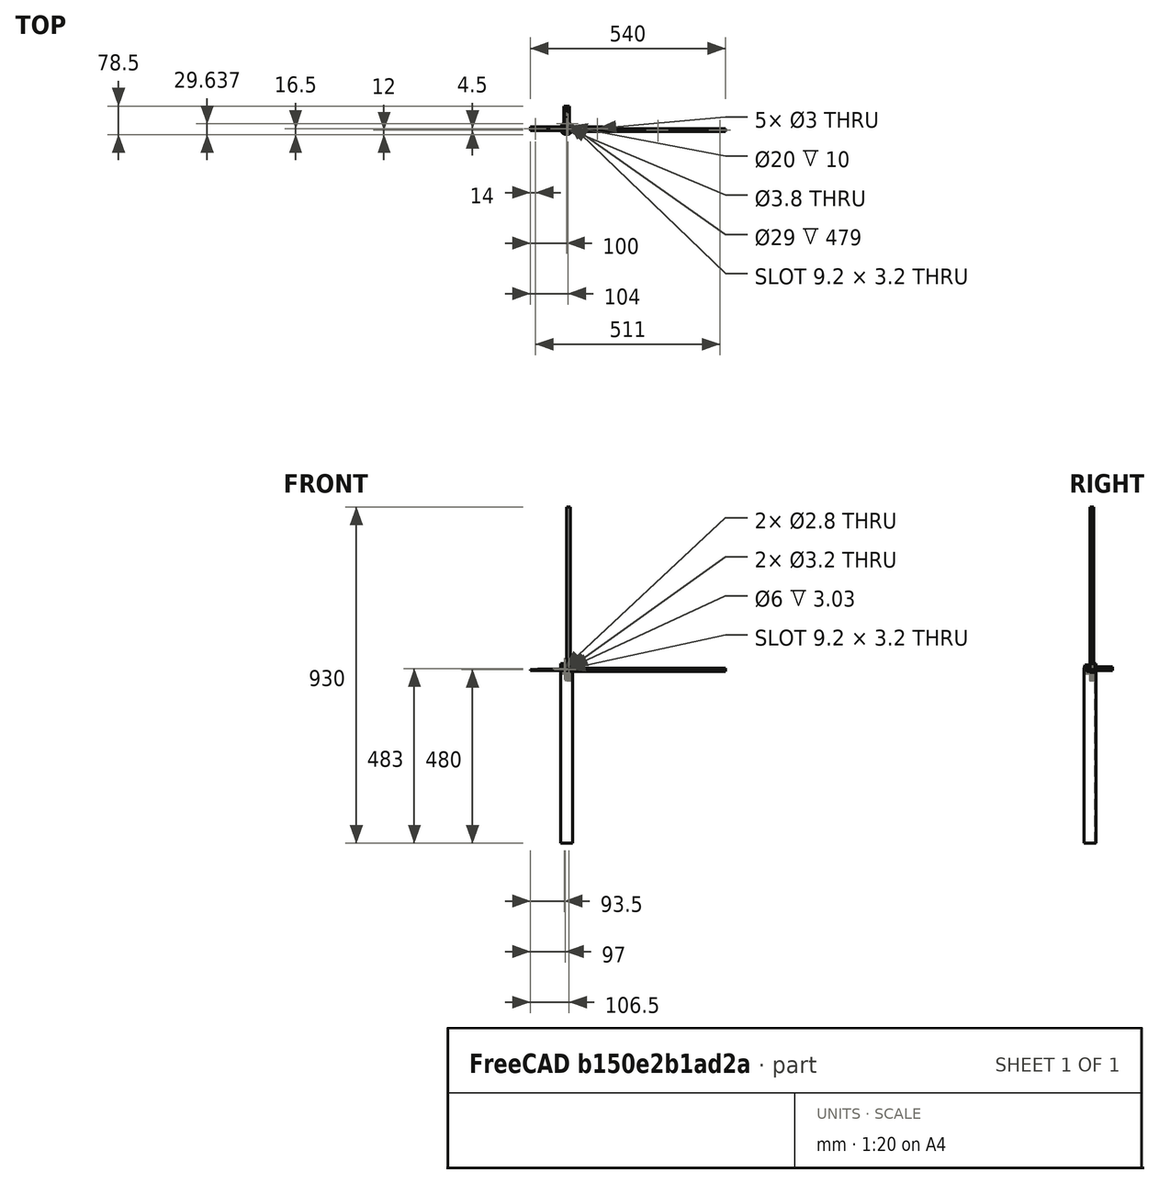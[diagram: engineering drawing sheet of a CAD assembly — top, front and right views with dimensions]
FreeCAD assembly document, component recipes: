
FREECAD ASSEMBLY — COMPONENT RECIPES ("angleBarLamp")

This assembly document has 14 components, labeled P0..P13 below (a component is one placed body or linked part). 13 of them carry a construction recipe — the FreeCAD feature program that regenerates the part from scratch, quoted from this document or its linked companion documents; the rest are supplied as boundary geometry only. No exploded tour is included for this assembly.
COMPONENT P0 — geometry summary ("Assembly"; no construction recipe available for this part):
  bounding box: 1011.0 x 58.0 x 58.0 mm
  tessellated surface: 14,300 triangles
  volume: 263663 mm^3 (8% of its bounding box)
COMPONENT P1 — recipe-attached ("b_cableClip", modeled in this document).
Construction recipe (the document's own serialized feature program — sketch geometry with constraints, then the solid features built on it; lengths are millimeters unless a unit is written):

FEATURE [PartDesign::CoordinateSystem] LCS_1
  AttacherType = Attacher::AttachEngine3D
  MapMode = 2
  Support = -> [X_Axis028]
FEATURE [Sketcher::SketchObject] Sketch028  label="sk_cableClipProfile"
  FullyConstrained = true
  MapMode = 5
  Support = -> [XY_Plane028]
  sketch-geometry (30):
    g0: LineSegment StartX=0 StartY=0 StartZ=0 EndX=0 EndY=10.1 EndZ=0
    g1: LineSegment StartX=0 StartY=10.1 StartZ=0 EndX=1.2 EndY=10.1 EndZ=0
    g2: LineSegment StartX=1.2 StartY=10.1 StartZ=0 EndX=1.2 EndY=1.2 EndZ=0
    g3: LineSegment StartX=1.2 StartY=1.2 StartZ=0 EndX=10.1 EndY=1.2 EndZ=0
    g4: LineSegment StartX=10.1 StartY=1.2 StartZ=0 EndX=10.1 EndY=0 EndZ=0
    g5: LineSegment StartX=10.1 StartY=0 StartZ=0 EndX=0 EndY=0 EndZ=0
    g6: LineSegment StartX=6.1 StartY=1.2 StartZ=0 EndX=6.1 EndY=2.7 EndZ=0
    g7: LineSegment StartX=6.1 StartY=2.7 StartZ=0 EndX=11.6 EndY=2.7 EndZ=0
    g8: LineSegment StartX=11.6 StartY=2.7 StartZ=0 EndX=11.6 EndY=-1.5 EndZ=0
    g9: LineSegment StartX=11.6 StartY=-1.5 StartZ=0 EndX=10.05 EndY=-1.5 EndZ=0
    g10: LineSegment StartX=-1.5 StartY=-1.5 StartZ=0 EndX=-1.5 EndY=5 EndZ=0
    g11: LineSegment StartX=-1.5 StartY=5 StartZ=0 EndX=0 EndY=5 EndZ=0
    g12: LineSegment StartX=0 StartY=5 StartZ=0 EndX=0 EndY=0 EndZ=0
    g13: LineSegment StartX=0 StartY=0 StartZ=0 EndX=1.55 EndY=0 EndZ=0
    g14: LineSegment StartX=10.1 StartY=0 StartZ=0 EndX=10.1 EndY=1.2 EndZ=0
    g15: LineSegment StartX=10.1 StartY=1.2 StartZ=0 EndX=6.1 EndY=1.2 EndZ=0
    g16: LineSegment StartX=-1.5 StartY=-1.5 StartZ=0 EndX=0 EndY=0 EndZ=0
    g17: LineSegment StartX=11.6 StartY=2.7 StartZ=0 EndX=10.1 EndY=1.2 EndZ=0
    g18: LineSegment StartX=1.55 StartY=0 StartZ=0 EndX=1.55 EndY=-2.5 EndZ=0
    g19: LineSegment StartX=1.55 StartY=-2.5 StartZ=0 EndX=8.55 EndY=-2.5 EndZ=0
    g20: LineSegment StartX=8.55 StartY=-2.5 StartZ=0 EndX=8.55 EndY=0 EndZ=0
    g21: LineSegment StartX=10.05 StartY=-1.5 StartZ=0 EndX=10.05 EndY=-4 EndZ=0
    g22: LineSegment StartX=10.05 StartY=-4 StartZ=0 EndX=0.05 EndY=-4 EndZ=0
    g23: LineSegment StartX=0.05 StartY=-4 StartZ=0 EndX=0.05 EndY=-1.5 EndZ=0
    g24: LineSegment StartX=8.55 StartY=0 StartZ=0 EndX=10.1 EndY=0 EndZ=0
    g25: LineSegment StartX=0.05 StartY=-1.5 StartZ=0 EndX=-1.5 EndY=-1.5 EndZ=0
    g26: LineSegment StartX=0.05 StartY=-1.5 StartZ=0 EndX=1.55 EndY=0 EndZ=0
    g27: LineSegment StartX=8.55 StartY=0 StartZ=0 EndX=10.05 EndY=-1.5 EndZ=0
    g28: LineSegment StartX=8.55 StartY=-2.5 StartZ=0 EndX=10.05 EndY=-4 EndZ=0
    g29: LineSegment StartX=0.05 StartY=-4 StartZ=0 EndX=1.55 EndY=-2.5 EndZ=0
  constraints (78):
    c: Coincident(g0,g1)
    c: Coincident(g1,g2)
    c: Coincident(g2,g3)
    c: Coincident(g3,g4)
    c: Coincident(g4,g5)
    c: Coincident(g0,g5)
    c: Coincident(g0,g-1)
    c: Horizontal(g1)
    c: Horizontal(g3)
    c: Horizontal(g5)
    c: Vertical(g0)
    c: Vertical(g2)
    c: Vertical(g4)
    c: Equal(g1,g4)
    c: Equal(g5,g0)
    c: DistanceX(g5,g5) = 10.1
    c: DistanceY(g4,g4) = 1.2
    c: Coincident(g6,g7)
    c: Coincident(g7,g8)
    c: Coincident(g8,g9)
    c: Coincident(g25,g10)
    c: Coincident(g10,g11)
    c: Coincident(g11,g12)
    c: Coincident(g12,g13)
    c: Coincident(g24,g14)
    c: Coincident(g14,g15)
    c: Coincident(g15,g6)
    c: Coincident(g3,g14)
    c: Coincident(g4,g24)
    c: PointOnObject(g6,g3)
    c: PointOnObject(g11,g0)
    c: Coincident(g0,g12)
    c: Vertical(g8)
    c: Vertical(g6)
    c: Horizontal(g9)
    c: Horizontal(g11)
    c: Horizontal(g7)
    c: Equal(g11,g6)
    c: DistanceX(g11,g11) = 1.5
    c: Vertical(g10)
    c: Coincident(g17,g14)
    c: Coincident(g17,g7)
    c: Angle(g7,g17) = 0.785398
    c: Angle(g16,g10) = 0.785398
    c: Coincident(g25,g16)
    c: Coincident(g0,g16)
    c: DistanceX(g15,g15) = 4
    c: DistanceY(g12,g12) = 5
    c: Coincident(g18,g19)
    c: Coincident(g19,g20)
    c: Coincident(g21,g22)
    c: Coincident(g22,g23)
    c: Coincident(g13,g18)
    c: Coincident(g24,g20)
    c: Tangent(g13,g24)
    c: Coincident(g9,g21)
    c: Tangent(g9,g25)
    c: Vertical(g23)
    c: Vertical(g18)
    c: Vertical(g20)
    c: Vertical(g21)
    c: Horizontal(g19)
    c: Horizontal(g22)
    c: DistanceX(g19,g19) = 7
    c: Coincident(g18,g29)
    c: Coincident(g22,g29)
    c: Coincident(g19,g28)
    c: Coincident(g21,g28)
    c: Coincident(g20,g27)
    c: Coincident(g9,g27)
    c: Parallel(g16,g26)
    c: Parallel(g26,g29)
    c: Coincident(g13,g26)
    c: Coincident(g23,g25)
    c: Coincident(g23,g26)
    c: Angle(g28,g22) = 0.785398
    c: Equal(g13,g24)
    c: DistanceY(g20,g20) = 2.5
FEATURE [PartDesign::Pad] Pad010  label="cableClipExtrude"
  AllowMultiFace = false
  Direction = (1,1,1)
  Length = 10
  Length2 = 100
  Profile = -> Sketch028
  Refine = true
  Type = 0
FEATURE [PartDesign::Fillet] Fillet002  label="cableClipFillet"
  Base = -> Pad010 [Edge23,Edge17,Edge14,Edge8,Edge11,Edge5,Edge26,Edge2,Edge20]
  BaseFeature = -> Pad010
  Radius = 0.5
  Refine = true
  SupportTransform = true
  UseAllEdges = false
FEATURE [PartDesign::Body] Body  label="b_cableClip"
  Group = -> [Sketch028,Pad010,Fillet002,LCS_1]
  Origin = -> Origin028
  Tip = -> Fillet002
COMPONENT P2 — recipe-attached ("template_L-profile_10mm_foot", modeled in this document).
Construction recipe (the document's own serialized feature program — sketch geometry with constraints, then the solid features built on it; lengths are millimeters unless a unit is written):

FEATURE [PartDesign::CoordinateSystem] LCS_angleBar10  label="LCS_Lprofile10"
  AttacherType = Attacher::AttachEngine3D
  MapMode = 2
  Support = -> [X_Axis006]
FEATURE [Sketcher::SketchObject] Sketch017  label="sk_L-profile10mm"
  FullyConstrained = false
  MapMode = 5
  Support = -> [XY_Plane006]
  sketch-geometry (6):
    g0: LineSegment StartX=0 StartY=0 StartZ=0 EndX=0 EndY=10.1 EndZ=0
    g1: LineSegment StartX=0 StartY=10.1 StartZ=0 EndX=1.1 EndY=10.1 EndZ=0
    g2: LineSegment StartX=1.1 StartY=10.1 StartZ=0 EndX=1.1 EndY=1.1 EndZ=0
    g3: LineSegment StartX=1.1 StartY=1.1 StartZ=0 EndX=10.1 EndY=1.1 EndZ=0
    g4: LineSegment StartX=10.1 StartY=1.1 StartZ=0 EndX=10.1 EndY=0 EndZ=0
    g5: LineSegment StartX=10.1 StartY=0 StartZ=0 EndX=0 EndY=0 EndZ=0
  constraints (17):
    c: Coincident(g-1,g0)
    c: PointOnObject(g0,g-2)
    c: Coincident(g0,g1)
    c: Horizontal(g1)
    c: Coincident(g1,g2)
    c: Vertical(g2)
    c: Coincident(g2,g3)
    c: Horizontal(g3)
    c: Coincident(g3,g4)
    c: Coincident(g4,g5)
    c: Coincident(g5,g0)
    c: Horizontal(g5)
    c: Vertical(g4)
    c: DistanceY(g0,g0) = 10.1
    c: Equal(g0,g5)
    c: DistanceX(g1,g1) = 1.1
    c: Equal(g1,g4)
FEATURE [PartDesign::Pad] Pad005  label="L-profile10mm"
  AllowMultiFace = false
  Direction = (0,0,1)
  Length = 450
  Length2 = 100
  Profile = -> Sketch017
  Type = 0
  expr: Length = Spreadsheet.l_arms
FEATURE [PartDesign::Body] Body006  label="template_L-profile_10mm_foot"
  Group = -> [Sketch017,Pad005,LCS_angleBar10]
  Origin = -> Origin006
  Tip = -> Pad005
COMPONENT P3 — recipe-attached ("b_base_cap", modeled in this document).
Construction recipe (the document's own serialized feature program — sketch geometry with constraints, then the solid features built on it; lengths are millimeters unless a unit is written):

FEATURE [PartDesign::CoordinateSystem] LCS_bottom_blog
  AttacherType = Attacher::AttachEngine3D
  AttachmentOffset = pos=(5,0,0) rot=(0,0,1;0rad)
  MapMode = 2
  Placement = pos=(1.1e-15,1.1e-15,5) rot=(0.57735,-0.57735,0.57735;2.0944rad)
  Support = -> [Z_Axis030]
FEATURE [Sketcher::SketchObject] Sketch001
  FullyConstrained = false
  MapMode = 5
  Placement = pos=(0,0,0) rot=(1,0,0;1.5708rad)
  Support = -> [XZ_Plane001]
  sketch-geometry (4):
    g0: LineSegment StartX=0 StartY=28.2609 StartZ=0 EndX=10 EndY=28.2609 EndZ=0
    g1: LineSegment StartX=10 StartY=28.2609 StartZ=0 EndX=10 EndY=3 EndZ=0
    g2: LineSegment StartX=10 StartY=3 StartZ=0 EndX=0 EndY=3 EndZ=0
    g3: LineSegment StartX=0 StartY=3 StartZ=0 EndX=0 EndY=28.2609 EndZ=0
  constraints (11):
    c: Coincident(g0,g1)
    c: Coincident(g1,g2)
    c: Coincident(g2,g3)
    c: Coincident(g3,g0)
    c: Horizontal(g0)
    c: Horizontal(g2)
    c: Vertical(g1)
    c: Vertical(g3)
    c: PointOnObject(g0,g-2)
    c: DistanceY(g1) = 3
    c: DistanceX(g0,g0) = 10
FEATURE [Sketcher::SketchObject] Sketch052
  FullyConstrained = true
  MapMode = 5
  Placement = pos=(0,0,0) rot=(1,0,0;1.5708rad)
  Support = -> [XZ_Plane001]
  sketch-geometry (6):
    g0: LineSegment StartX=0 StartY=0 StartZ=0 EndX=16.25 EndY=0 EndZ=0
    g1: LineSegment StartX=16.25 StartY=0 StartZ=0 EndX=16.25 EndY=5 EndZ=0
    g2: LineSegment StartX=16.25 StartY=5 StartZ=0 EndX=15 EndY=5 EndZ=0
    g3: LineSegment StartX=15 StartY=5 StartZ=0 EndX=15 EndY=13 EndZ=0
    g4: LineSegment StartX=15 StartY=13 StartZ=0 EndX=0 EndY=13 EndZ=0
    g5: LineSegment StartX=0 StartY=13 StartZ=0 EndX=0 EndY=0 EndZ=0
  constraints (17):
    c: Coincident(g-1,g0)
    c: Horizontal(g0)
    c: Coincident(g0,g1)
    c: Coincident(g1,g2)
    c: Horizontal(g2)
    c: Coincident(g2,g3)
    c: Coincident(g3,g4)
    c: Horizontal(g4)
    c: Coincident(g4,g5)
    c: Coincident(g5,g0)
    c: Vertical(g5)
    c: Vertical(g1)
    c: Vertical(g3)
    c: DistanceY(g3,g3) = 8
    c: DistanceY(g1,g1) = 5
    c: DistanceX(g4,g4) = 15
    c: DistanceX(g0,g0) = 16.25
FEATURE [PartDesign::Revolution] Revolution001
  Angle = 360
  Axis = (0,2e-16,1)
  Base = (0,0,0)
  Placement = pos=(0,0,0) rot=(1,0,0;1.5708rad)
  Profile = -> Sketch052
  ReferenceAxis = -> Sketch052 [V_Axis]
  Reversed = true
FEATURE [PartDesign::Chamfer] Chamfer001
  Angle = 3
  Base = -> Revolution001 [Edge5]
  BaseFeature = -> Revolution001
  ChamferType = 2
  FlipDirection = false
  Placement = pos=(0,0,0) rot=(1,0,0;1.5708rad)
  Size = 7
  Size2 = 1
  SupportTransform = false
  UseAllEdges = false
FEATURE [PartDesign::Groove] Groove001
  Angle = 360
  Axis = (0,2e-16,1)
  Base = (0,0,0)
  BaseFeature = -> Chamfer001
  Placement = pos=(0,0,0) rot=(1,0,0;1.5708rad)
  Profile = -> Sketch001
  ReferenceAxis = -> Sketch001 [V_Axis]
FEATURE [PartDesign::Body] Body015  label="b_base_cap"
  Group = -> [Sketch052,Revolution001,Chamfer001,Sketch001,Groove001,LCS_bottom_blog]
  Origin = -> Origin030
  Tip = -> Groove001
COMPONENT P4 — recipe-attached ("b_LProfile_8mm", modeled in this document).
Construction recipe (the document's own serialized feature program — sketch geometry with constraints, then the solid features built on it; lengths are millimeters unless a unit is written):

FEATURE [PartDesign::CoordinateSystem] LCS_1004  label="LCS_screwaxis"
  AttacherType = Attacher::AttachEngine3D
  MapMode = 2
  Support = -> [X_Axis031]
  expr: .AttachmentOffset.Base.x = Variables.time < Variables.motion2_start ? 0 : (Variables.time < Variables.motion3_start ? -Spreadsheet.l_sliding_hole * (Variables.time - Variables.motion2_start) / Variables.motion2_duration : -Spreadsheet.l_sliding_hole)
FEATURE [Sketcher::SketchObject] Sketch053
  FullyConstrained = true
  MapMode = 5
  Placement = pos=(0,0,0) rot=(0.57735,0.57735,0.57735;2.0944rad)
  Support = -> [YZ_Plane031]
  sketch-geometry (6):
    g0: LineSegment StartX=0 StartY=-4.5 StartZ=0 EndX=-8 EndY=-4.5 EndZ=0
    g1: LineSegment StartX=-8 StartY=-4.5 StartZ=0 EndX=-8 EndY=-3.5 EndZ=0
    g2: LineSegment StartX=-8 StartY=-3.5 StartZ=0 EndX=-1 EndY=-3.5 EndZ=0
    g3: LineSegment StartX=-1 StartY=-3.5 StartZ=0 EndX=-1 EndY=3.5 EndZ=0
    g4: LineSegment StartX=-1 StartY=3.5 StartZ=0 EndX=0 EndY=3.5 EndZ=0
    g5: LineSegment StartX=0 StartY=3.5 StartZ=0 EndX=0 EndY=-4.5 EndZ=0
  constraints (17):
    c: PointOnObject(g0,g-2)
    c: Horizontal(g0)
    c: Coincident(g0,g1)
    c: Coincident(g1,g2)
    c: Coincident(g2,g3)
    c: Coincident(g3,g4)
    c: PointOnObject(g4,g-2)
    c: Horizontal(g4)
    c: Coincident(g4,g5)
    c: Coincident(g5,g0)
    c: Equal(g1,g4)
    c: Vertical(g1)
    c: Equal(g0,g5)
    c: DistanceY(g5,g5) = 8
    c: DistanceY(g1,g1) = 1
    c: Horizontal(g2)
    c: Symmetric(g2,g3,g-1)
FEATURE [PartDesign::Pad] Pad017
  Direction = (1,-2e-16,3e-16)
  Length = 440
  Length2 = 16
  Placement = pos=(0,0,0) rot=(0.57735,0.57735,0.57735;2.0944rad)
  Profile = -> Sketch053
  ReferenceAxis = -> Sketch053 [N_Axis]
  Type = 4
FEATURE [Sketcher::SketchObject] Sketch054
  FullyConstrained = true
  MapMode = 5
  Placement = pos=(0,0,0) rot=(1,0,0;1.5708rad)
  Support = -> [XZ_Plane031]
  sketch-geometry (11):
    g0: ArcOfCircle CenterX=-6 CenterY=-1e-16 CenterZ=0 NormalX=0 NormalY=0 NormalZ=1 AngleXU=0 Radius=1.6 StartAngle=1.5708 EndAngle=4.71239
    g1: ArcOfCircle CenterX=0 CenterY=0 CenterZ=0 NormalX=0 NormalY=0 NormalZ=1 AngleXU=0 Radius=1.6 StartAngle=4.71239 EndAngle=7.85398
    g2: LineSegment StartX=-6 StartY=-1.6 StartZ=0 EndX=0 EndY=-1.6 EndZ=0
    g3: LineSegment StartX=5e-16 StartY=1.6 StartZ=0 EndX=-6 EndY=1.6 EndZ=0
    g4: LineSegment StartX=-16.5 StartY=4 StartZ=0 EndX=-10.5 EndY=4 EndZ=0
    g5: LineSegment StartX=-10.5 StartY=4 StartZ=0 EndX=-11.436 EndY=-0.3375 EndZ=0
    g6: ArcOfCircle CenterX=-13 CenterY=-1e-16 CenterZ=0 NormalX=0 NormalY=0 NormalZ=1 AngleXU=0 Radius=1.6 StartAngle=3.14159 EndAngle=6.07065
    g7: LineSegment StartX=-14.6 StartY=-6e-16 StartZ=0 EndX=-14.6 EndY=1.25 EndZ=0
    g8: ArcOfCircle CenterX=-15.1 CenterY=1.25 CenterZ=0 NormalX=0 NormalY=0 NormalZ=1 AngleXU=0 Radius=0.5 StartAngle=1e-16 EndAngle=1.75335
    g9: LineSegment StartX=-15.1908 StartY=1.74169 StartZ=0 EndX=-16.5 EndY=1.5 EndZ=0
    g10: LineSegment StartX=-16.5 StartY=1.5 StartZ=0 EndX=-16.5 EndY=4 EndZ=0
  constraints (28):
    c: Tangent(g0,g2) = -1.5708
    c: Tangent(g2,g1) = -1.5708
    c: Tangent(g1,g3) = -1.5708
    c: Tangent(g3,g0) = -1.5708
    c: Equal(g0,g1)
    c: Horizontal(g2)
    c: DistanceX(g3,g3) = 6
    c: Radius(g1) = 1.6
    c: Horizontal(g4)
    c: Coincident(g4,g5)
    c: Tangent(g5,g6) = 1.5708
    c: Tangent(g6,g7) = 1.5708
    c: Tangent(g7,g8) = -1.5708
    c: Coincident(g9,g10)
    c: Coincident(g10,g4)
    c: Vertical(g10)
    c: Vertical(g7)
    c: Radius(g6) = 1.6
    c: Tangent(g8,g9) = -1.5708
    c: Radius(g8) = 0.5
    c: DistanceY(g6,g8) = 1.25
    c: DistanceY(g8,g9) = 0.25
    c: Horizontal(g0,g6)
    c: DistanceX(g6,g0) = 7
    c: DistanceX(g6,g4) = 2.5
    c: DistanceX(g9,g6) = 3.5
    c: Coincident(g1,g-1)
    c: DistanceY(g6,g4) = 4
FEATURE [PartDesign::Pocket] Pocket018
  BaseFeature = -> Pad017
  Direction = (0,1,2e-16)
  Length = 5
  Length2 = 5
  Placement = pos=(0,0,0) rot=(0.57735,0.57735,0.57735;2.0944rad)
  Profile = -> Sketch054
  ReferenceAxis = -> Sketch054 [N_Axis]
  Reversed = true
  Type = 0
FEATURE [Sketcher::SketchObject] Sketch055
  FullyConstrained = true
  MapMode = 5
  Support = -> [XY_Plane031]
  expr: Constraints[2] = Spreadsheet.led_screw_offset
  expr: Constraints[5] = Spreadsheet.led_screw_pos
  sketch-geometry (2):
    g0: Circle CenterX=425 CenterY=-4.5 CenterZ=0 NormalX=0 NormalY=0 NormalZ=1 AngleXU=0 Radius=1.5
    g1: Circle CenterX=253 CenterY=-4.5 CenterZ=0 NormalX=0 NormalY=0 NormalZ=1 AngleXU=0 Radius=1.5
  constraints (6):
    c: Horizontal(g1,g0)
    c: Equal(g0,g1)
    c: DistanceX(g1,g0) = 172
    c: Diameter(g1) = 3
    c: DistanceY(g0,g-1) = 4.5
    c: DistanceX(g0) = 425
FEATURE [PartDesign::Pocket] Pocket019
  BaseFeature = -> Pocket018
  Direction = (0,0,-1)
  Length = 5
  Length2 = 5
  Placement = pos=(0,0,0) rot=(0.57735,0.57735,0.57735;2.0944rad)
  Profile = -> Sketch055
  ReferenceAxis = -> Sketch055 [N_Axis]
  Type = 0
FEATURE [PartDesign::CoordinateSystem] LCS_ledscrew
  AttacherType = Attacher::AttachEngine3D
  AttachmentOffset = pos=(425,-4.5,-4.5) rot=(0,0,1;0rad)
  MapMode = 2
  Placement = pos=(425,-4.5,-4.5) rot=(0,0,1;0rad)
  Support = -> [X_Axis031]
  expr: .AttachmentOffset.Base.x = Spreadsheet.led_screw_pos
FEATURE [PartDesign::Body] b_LProfile_8mm
  Group = -> [LCS_1004,Sketch053,Pad017,Sketch054,Pocket018,Sketch055,Pocket019,LCS_ledscrew]
  Origin = -> Origin031
  Tip = -> Pocket019
COMPONENT P5 — recipe-attached ("b_nut", modeled in this document).
Construction recipe (the document's own serialized feature program — sketch geometry with constraints, then the solid features built on it; lengths are millimeters unless a unit is written):

FEATURE [PartDesign::CoordinateSystem] LCS_0001
  AttacherType = Attacher::AttachEngine3D
  MapMode = 2
  Support = -> [X_Axis002]
FEATURE [Sketcher::SketchObject] Sketch037
  FullyConstrained = true
  MapMode = 5
  Placement = pos=(0,0,0) rot=(1,0,0;1.5708rad)
  Support = -> [XZ_Plane003]
  sketch-geometry (6):
    g0: LineSegment StartX=6.1 StartY=0.5 StartZ=0 EndX=6.1 EndY=2.8 EndZ=0
    g1: LineSegment StartX=6.1 StartY=0.5 StartZ=0 EndX=3 EndY=0.5 EndZ=0
    g2: LineSegment StartX=3 StartY=0.5 StartZ=0 EndX=3 EndY=0 EndZ=0
    g3: LineSegment StartX=6.1 StartY=2.8 StartZ=0 EndX=1.5 EndY=2.8 EndZ=0
    g4: LineSegment StartX=1.5 StartY=2.8 StartZ=0 EndX=1.5 EndY=0 EndZ=0
    g5: LineSegment StartX=1.5 StartY=0 StartZ=0 EndX=3 EndY=0 EndZ=0
  constraints (18):
    c: Vertical(g0)
    c: DistanceX(g-1,g0) = 6.1
    c: DistanceY(g0,g0) = 2.3
    c: Coincident(g0,g1)
    c: Horizontal(g1)
    c: Coincident(g1,g2)
    c: Vertical(g2)
    c: DistanceX(g-1,g2) = 3
    c: Coincident(g0,g3)
    c: Horizontal(g3)
    c: Coincident(g3,g4)
    c: Vertical(g4)
    c: Coincident(g4,g5)
    c: Coincident(g5,g2)
    c: Horizontal(g5)
    c: DistanceY(g4,g4) = 2.8
    c: DistanceX(g-1,g4) = 1.5
    c: PointOnObject(g4,g-1)
FEATURE [PartDesign::Revolution] Revolution
  Angle = 360
  Axis = (0,-2e-16,1)
  Base = (0,0,0)
  Placement = pos=(0,0,0) rot=(1,0,0;1.5708rad)
  Profile = -> Sketch037
  ReferenceAxis = -> Sketch037 [V_Axis]
  Reversed = true
FEATURE [Sketcher::SketchObject] Sketch038
  FullyConstrained = false
  MapMode = 5
  Support = -> [XY_Plane002]
  sketch-geometry (1):
    g0: Circle CenterX=0 CenterY=6.12912 CenterZ=0 NormalX=0 NormalY=0 NormalZ=1 AngleXU=0 Radius=0.15
  constraints (2):
    c: PointOnObject(g0,g-2)
    c: Radius(g0) = 0.15
FEATURE [PartDesign::Pocket] Pocket011
  BaseFeature = -> Revolution
  Direction = (1,1,1)
  Length = 5
  Length2 = 100
  Placement = pos=(0,0,0) rot=(1,0,0;1.5708rad)
  Profile = -> Sketch038
  Reversed = true
  Type = 1
FEATURE [PartDesign::PolarPattern] PolarPattern
  Angle = 360
  Axis = -> Sketch038 [N_Axis]
  BaseFeature = -> Pocket011
  Occurrences = 100
  Originals = -> [Pocket011]
  Placement = pos=(0,0,0) rot=(1,0,0;1.5708rad)
FEATURE [PartDesign::Body] b_nut
  Group = -> [LCS_0001,Sketch037,Revolution,Sketch038,Pocket011,PolarPattern]
  Origin = -> Origin002
  Tip = -> PolarPattern
COMPONENT P6 — recipe-attached ("b_spacer", modeled in this document).
Construction recipe (the document's own serialized feature program — sketch geometry with constraints, then the solid features built on it; lengths are millimeters unless a unit is written):

FEATURE [PartDesign::CoordinateSystem] LCS_0003
  AttacherType = Attacher::AttachEngine3D
  MapMode = 2
  Support = -> [X_Axis022]
FEATURE [Sketcher::SketchObject] Sketch034
  FullyConstrained = false
  MapMode = 5
  Support = -> [XY_Plane022]
  sketch-geometry (6):
    g0: Circle CenterX=0 CenterY=0 CenterZ=0 NormalX=0 NormalY=0 NormalZ=1 AngleXU=0 Radius=1.9
    g1: Circle CenterX=0 CenterY=0 CenterZ=0 NormalX=0 NormalY=0 NormalZ=1 AngleXU=0 Radius=2.7
    g2: LineSegment StartX=-2.74547 StartY=3.8 StartZ=0 EndX=7.25453 EndY=3.8 EndZ=0
    g3: LineSegment StartX=7.25453 StartY=3.8 StartZ=0 EndX=7.25453 EndY=-2.7 EndZ=0
    g4: LineSegment StartX=7.25453 StartY=-2.7 StartZ=0 EndX=-2.74547 EndY=-2.7 EndZ=0
    g5: LineSegment StartX=-2.74547 StartY=-2.7 StartZ=0 EndX=-2.74547 EndY=3.8 EndZ=0
  constraints (15):
    c: Coincident(g0,g-1)
    c: Coincident(g1,g0)
    c: Radius(g0) = 1.9
    c: Radius(g1) = 2.7
    c: Coincident(g2,g3)
    c: Coincident(g3,g4)
    c: Coincident(g4,g5)
    c: Coincident(g5,g2)
    c: Horizontal(g2)
    c: Horizontal(g4)
    c: Vertical(g3)
    c: Vertical(g5)
    c: DistanceY(g3,g3) = 6.5
    c: DistanceY(g4,g0) = 2.7
    c: DistanceX(g2,g2) = 10
FEATURE [PartDesign::Pad] Pad013
  Direction = (1,1,1)
  Length = 6.5
  Length2 = 100
  Profile = -> Sketch034
  Type = 0
FEATURE [PartDesign::Body] b_spacer
  Group = -> [LCS_0003,Sketch034,Pad013]
  Origin = -> Origin022
  Tip = -> Pad013
COMPONENT P7 — recipe-attached ("b_stencil", modeled in this document).
Construction recipe (the document's own serialized feature program — sketch geometry with constraints, then the solid features built on it; lengths are millimeters unless a unit is written):

FEATURE [PartDesign::CoordinateSystem] LCS_0005
  AttacherType = Attacher::AttachEngine3D
  MapMode = 2
  Support = -> [X_Axis024]
FEATURE [PartDesign::ShapeBinder] ShapeBinder
  Placement = pos=(0,0,1) rot=(0,0,1;3.14159rad)
  Support = -> [Sketch048]
  TraceSupport = false
FEATURE [Sketcher::SketchObject] Sketch049
  FullyConstrained = false
  MapMode = 5
  Placement = pos=(0,0,0) rot=(1,0,0;1.5708rad)
  Support = -> [XZ_Plane024]
  sketch-geometry (6):
    g0: LineSegment StartX=0 StartY=8 StartZ=0 EndX=0 EndY=0 EndZ=0
    g1: LineSegment StartX=0 StartY=0 StartZ=0 EndX=8 EndY=0 EndZ=0
    g2: LineSegment StartX=8 StartY=0 StartZ=0 EndX=8 EndY=-2.47577 EndZ=0
    g3: LineSegment StartX=8 StartY=-2.47577 StartZ=0 EndX=-7.32977 EndY=-2.47577 EndZ=0
    g4: LineSegment StartX=-7.32977 StartY=-2.47577 StartZ=0 EndX=-7.32977 EndY=8 EndZ=0
    g5: LineSegment StartX=-7.32977 StartY=8 StartZ=0 EndX=0 EndY=8 EndZ=0
  constraints (15):
    c: PointOnObject(g0,g-2)
    c: Coincident(g0,g-1)
    c: Coincident(g0,g1)
    c: PointOnObject(g1,g-1)
    c: Coincident(g1,g2)
    c: Vertical(g2)
    c: Coincident(g2,g3)
    c: Horizontal(g3)
    c: Coincident(g3,g4)
    c: Vertical(g4)
    c: Coincident(g4,g5)
    c: Coincident(g5,g0)
    c: Horizontal(g5)
    c: DistanceX(g1,g1) = 8
    c: Equal(g0,g1)
FEATURE [PartDesign::Pad] Pad014
  Direction = (1,1,1)
  Length = 62
  Length2 = 100
  Placement = pos=(0,0,0) rot=(1,0,0;1.5708rad)
  Profile = -> Sketch049
  Refine = true
  Reversed = true
  Type = 0
FEATURE [PartDesign::Pocket] Pocket017
  BaseFeature = -> Pad014
  Direction = (0,0,-1)
  Length = 5
  Length2 = 100
  Placement = pos=(0,0,0) rot=(1,0,0;1.5708rad)
  Profile = -> ShapeBinder
  Refine = true
  Type = 0
FEATURE [PartDesign::Body] b_stencil
  Group = -> [LCS_0005,ShapeBinder,Sketch049,Pad014,Pocket017]
  Origin = -> Origin024
  Tip = -> Pocket017
COMPONENT P8 — recipe-attached ("b_topBlockArmLock", modeled in this document).
Construction recipe (the document's own serialized feature program — sketch geometry with constraints, then the solid features built on it; lengths are millimeters unless a unit is written):

FEATURE [PartDesign::Plane] DatumPlane
  AttachmentOffset = pos=(0,0,12) rot=(0,0,1;0rad)
  Length = 60
  MapMode = 2
  Placement = pos=(4.7e-15,12,-4.7e-15) rot=(0.57735,0.57735,0.57735;4.18879rad)
  ResizeMode = 0
  Support = -> [Z_Axis001]
  Width = 60
FEATURE [PartDesign::CoordinateSystem] LCS_0
  AttacherType = Attacher::AttachEngine3D
  MapMode = 2
  Support = -> [X_Axis001]
FEATURE [Sketcher::SketchObject] Sketch
  FullyConstrained = true
  MapMode = 5
  Support = -> [XY_Plane001]
  expr: Constraints[16] = Spreadsheet.r_inner
  expr: Constraints[5] = Spreadsheet.w_topRail
  expr: Constraints[6] = Spreadsheet.w_wall_center / 2
  expr: Constraints[9] = Spreadsheet.r_outer
  sketch-geometry (7):
    g0: LineSegment StartX=-16.5 StartY=2e-15 StartZ=0 EndX=16.5 EndY=0 EndZ=0
    g1: ArcOfCircle CenterX=0 CenterY=0 CenterZ=0 NormalX=0 NormalY=0 NormalZ=1 AngleXU=0 Radius=16.5 StartAngle=0 EndAngle=2.22189
    g2: LineSegment StartX=-16.4829 StartY=0.75 StartZ=0 EndX=14.6058 EndY=0.75 EndZ=0
    g3: LineSegment StartX=11.6434 StartY=8.85 StartZ=0 EndX=-10 EndY=8.85 EndZ=0
    g4: LineSegment StartX=-10 StartY=8.85 StartZ=0 EndX=-10 EndY=13.1244 EndZ=0
    g5: ArcOfCircle CenterX=0 CenterY=0 CenterZ=0 NormalX=0 NormalY=0 NormalZ=1 AngleXU=0 Radius=16.5 StartAngle=3.09612 EndAngle=3.14159
    g6: ArcOfCircle CenterX=0 CenterY=0 CenterZ=0 NormalX=0 NormalY=0 NormalZ=1 AngleXU=0 Radius=14.625 StartAngle=0.0513046 EndAngle=0.649927
  constraints (20):
    c: PointOnObject(g0,g-1)
    c: Coincident(g1,g-1)
    c: Horizontal(g2)
    c: Horizontal(g3)
    c: Coincident(g3,g4)
    c: DistanceY(g2,g3) = 8.1
    c: DistanceY(g0,g2) = 0.75
    c: Vertical(g4)
    c: Symmetric(g0,g0,g1)
    c: Radius(g1) = 16.5
    c: Coincident(g1,g0)
    c: Coincident(g5,g1)
    c: Coincident(g5,g0)
    c: Coincident(g5,g2)
    c: Coincident(g6,g2)
    c: Coincident(g6,g3)
    c: Radius(g6) = 14.625
    c: Coincident(g1,g6)
    c: Coincident(g1,g4)
    c: DistanceX(g3,g1) = 10
FEATURE [PartDesign::Pad] Pad009
  Direction = (0,0,1)
  Length = 16
  Length2 = 7.5
  Profile = -> Sketch
  Type = 4
FEATURE [Sketcher::SketchObject] Sketch030
  FullyConstrained = true
  MapMode = 5
  Placement = pos=(0,0,0) rot=(1,0,0;1.5708rad)
  Support = -> [XZ_Plane002]
  expr: Constraints[6] = Spreadsheet.motionAngle
  sketch-geometry (3):
    g0: LineSegment StartX=6.5 StartY=-7.5 StartZ=0 EndX=-1.5 EndY=-7.5 EndZ=0
    g1: LineSegment StartX=-1.5 StartY=-7.5 StartZ=0 EndX=-1.5 EndY=-4.58824 EndZ=0
    g2: LineSegment StartX=-1.5 StartY=-4.58824 StartZ=0 EndX=6.5 EndY=-7.5 EndZ=0
  constraints (9):
    c: Horizontal(g0)
    c: DistanceY(g0,g-1) = 7.5
    c: Coincident(g0,g1)
    c: Vertical(g1)
    c: Coincident(g1,g2)
    c: Coincident(g0,g2)
    c: Angle(g2,g0) = 0.349066
    c: DistanceX(g0) = 6.5
    c: DistanceX(g0,g0) = 8
FEATURE [Sketcher::SketchObject] Sketch033
  FullyConstrained = false
  MapMode = 5
  Placement = pos=(4.7e-15,12,-4.7e-15) rot=(0.57735,0.57735,0.57735;4.18879rad)
  Support = -> [DatumPlane]
  expr: Constraints[0] = Spreadsheet.screw_offset
  sketch-geometry (5):
    g0: Circle CenterX=3 CenterY=-6.5 CenterZ=0 NormalX=0 NormalY=0 NormalZ=1 AngleXU=0 Radius=6.70275
    g1: LineSegment StartX=9.70763 StartY=-19.5547 StartZ=0 EndX=-3.70763 EndY=-19.5547 EndZ=0
    g2: LineSegment StartX=-3.70763 StartY=-19.5547 StartZ=0 EndX=-3.70763 EndY=-6.5 EndZ=0
    g3: ArcOfCircle CenterX=3 CenterY=-6.5 CenterZ=0 NormalX=0 NormalY=0 NormalZ=1 AngleXU=0 Radius=6.70763 StartAngle=2e-16 EndAngle=3.14159
    g4: LineSegment StartX=9.70763 StartY=-6.5 StartZ=0 EndX=9.70763 EndY=-19.5547 EndZ=0
  constraints (10):
    c: DistanceY(g0,g-1) = 6.5
    c: DistanceX(g0) = 3
    c: Horizontal(g1)
    c: Coincident(g1,g2)
    c: Vertical(g2)
    c: Tangent(g2,g3) = 1.5708
    c: Tangent(g3,g4) = 1.5708
    c: Coincident(g1,g4)
    c: Vertical(g4)
    c: Coincident(g3,g0)
FEATURE [PartDesign::Pocket] Pocket
  BaseFeature = -> Pad009
  Direction = (-4e-16,-1,4e-16)
  Length = 8
  Length2 = 100
  Profile = -> Sketch033
  Type = 0
FEATURE [Sketcher::SketchObject] Sketch036
  AttachmentOffset = pos=(0,0,-16.5) rot=(0,0,1;0rad)
  FullyConstrained = true
  MapMode = 5
  Placement = pos=(0,16.5,3.7e-15) rot=(1,0,0;1.5708rad)
  Support = -> [XZ_Plane002]
  expr: .AttachmentOffset.Base.z = -Spreadsheet.r_outer
  expr: Constraints[1] = Spreadsheet.screw_offset
  sketch-geometry (1):
    g0: Circle CenterX=6.5 CenterY=3 CenterZ=0 NormalX=0 NormalY=0 NormalZ=1 AngleXU=0 Radius=1.5
  constraints (3):
    c: DistanceY(g0) = 3
    c: DistanceX(g0) = 6.5
    c: Radius(g0) = 1.5
FEATURE [PartDesign::Hole] Hole
  BaseFeature = -> Pocket
  CustomThreadClearance = 0
  Depth = 25
  DepthType = 0
  Diameter = 3.2
  DrillForDepth = false
  DrillPoint = 1
  DrillPointAngle = 118
  HoleCutCountersinkAngle = 90
  HoleCutCustomValues = false
  HoleCutDepth = 3.4
  HoleCutDiameter = 6
  HoleCutType = 9
  ModelThread = false
  Profile = -> Sketch036
  Reversed = true
  Tapered = false
  TaperedAngle = 90
  ThreadClass = 0
  ThreadDepth = 23.5
  ThreadDepthType = 0
  ThreadDirection = 0
  ThreadFit = 1
  ThreadSize = 9
  ThreadType = 1
  Threaded = false
  UseCustomThreadClearance = false
FEATURE [Sketcher::SketchObject] Sketch045
  FullyConstrained = true
  MapMode = 5
  Placement = pos=(0,0,0) rot=(1,0,0;1.5708rad)
  Support = -> [XZ_Plane002]
  expr: Constraints[0] = Spreadsheet.screw_offset
  sketch-geometry (1):
    g0: Circle CenterX=-6.5 CenterY=3 CenterZ=0 NormalX=0 NormalY=0 NormalZ=1 AngleXU=0 Radius=1.4
  constraints (3):
    c: DistanceX(g0,g-1) = 6.5
    c: Radius(g0) = 1.4
    c: DistanceY(g0) = 3
FEATURE [PartDesign::Pocket] Pocket016
  BaseFeature = -> Hole
  Direction = (0,1,2e-16)
  Length = 16
  Length2 = 100
  Profile = -> Sketch045
  Refine = true
  Type = 0
FEATURE [PartDesign::Body] b_topBlockArmLock
  Group = -> [LCS_0,Sketch,Pad009,Sketch030,DatumPlane,Sketch033,Pocket,Sketch036,Hole,Sketch045,Pocket016]
  Origin = -> Origin001
  Tip = -> Pocket016
COMPONENT P9 — recipe-attached ("b_topBlockBase", modeled in this document).
Construction recipe (the document's own serialized feature program — sketch geometry with constraints, then the solid features built on it; lengths are millimeters unless a unit is written):

FEATURE [PartDesign::Plane] DatumPlane002
  AttachmentOffset = pos=(0,0,-12) rot=(0,0,1;0rad)
  Length = 60
  MapMode = 5
  Placement = pos=(0,0,-12) rot=(0,0,1;0rad)
  ResizeMode = 0
  Support = -> [XY_Plane021]
  Width = 60
  expr: .AttachmentOffset.Base.z = -Spreadsheet.h_topBlockBase
FEATURE [PartDesign::CoordinateSystem] LCS_0002
  AttacherType = Attacher::AttachEngine3D
  MapMode = 2
  Support = -> [X_Axis021]
FEATURE [Sketcher::SketchObject] Sketch031
  FullyConstrained = true
  MapMode = 5
  Support = -> [XY_Plane021]
  expr: Constraints[24] = Spreadsheet.w_wall_center / 2
  expr: Constraints[27] = Spreadsheet.r_outer
  expr: Constraints[6] = Spreadsheet.r_outer
  sketch-geometry (11):
    g0: ArcOfCircle CenterX=0 CenterY=0 CenterZ=0 NormalX=0 NormalY=0 NormalZ=1 AngleXU=0 Radius=16.5 StartAngle=6.23772 EndAngle=8.50508
    g1: ArcOfCircle CenterX=0 CenterY=0 CenterZ=0 NormalX=0 NormalY=0 NormalZ=1 AngleXU=0 Radius=16.5 StartAngle=3.09612 EndAngle=5.36349
    g2: LineSegment StartX=16.4829 StartY=-0.75 StartZ=0 EndX=2.5 EndY=-0.75 EndZ=0
    g3: LineSegment StartX=-16.4829 StartY=0.75 StartZ=0 EndX=-2.5 EndY=0.75 EndZ=0
    g4: LineSegment StartX=-2.5 StartY=0.75 StartZ=0 EndX=-2.5 EndY=8.85 EndZ=0
    g5: LineSegment StartX=-2.5 StartY=8.85 StartZ=0 EndX=-10 EndY=8.85 EndZ=0
    g6: LineSegment StartX=-10 StartY=8.85 StartZ=0 EndX=-10 EndY=13.1244 EndZ=0
    g7: LineSegment StartX=10 StartY=-13.1244 StartZ=0 EndX=10 EndY=-8.85 EndZ=0
    g8: LineSegment StartX=10 StartY=-8.85 StartZ=0 EndX=2.5 EndY=-8.85 EndZ=0
    g9: LineSegment StartX=2.5 StartY=-8.85 StartZ=0 EndX=2.5 EndY=-0.75 EndZ=0
    g10: Circle CenterX=0 CenterY=0 CenterZ=0 NormalX=0 NormalY=0 NormalZ=1 AngleXU=0 Radius=16.5
  constraints (30):
    c: Coincident(g0,g-1)
    c: Coincident(g1,g0)
    c: Symmetric(g0,g1,g0)
    c: Coincident(g3,g1)
    c: DistanceX(g2) = 2.5
    c: Symmetric(g2,g3,g0)
    c: Radius(g1) = 16.5
    c: Coincident(g3,g4)
    c: Vertical(g4)
    c: Coincident(g4,g5)
    c: Horizontal(g5)
    c: Coincident(g5,g6)
    c: Vertical(g6)
    c: DistanceX(g5,g0) = 10
    c: Vertical(g7)
    c: Coincident(g7,g8)
    c: Horizontal(g8)
    c: Coincident(g8,g9)
    c: Coincident(g9,g2)
    c: Vertical(g9)
    c: Equal(g9,g4)
    c: Horizontal(g2)
    c: Coincident(g0,g2)
    c: Horizontal(g3)
    c: DistanceY(g3) = 0.75
    c: DistanceY(g9,g9) = 8.1
    c: Coincident(g10,g0)
    c: Radius(g10) = 16.5
    c: Coincident(g1,g7)
    c: Coincident(g0,g6)
FEATURE [PartDesign::Pad] Pad011
  Direction = (0,0,1)
  Length = 12
  Length2 = 100
  Profile = -> Sketch031
  Reversed = true
  Type = 0
  expr: Length = Spreadsheet.h_topBlockBase
FEATURE [Sketcher::SketchObject] Sketch032
  AttachmentOffset = pos=(0,0,-0.6) rot=(0,0,1;0rad)
  FullyConstrained = false
  MapMode = 5
  Placement = pos=(0,0,-0.6) rot=(0,0,1;0rad)
  Support = -> [XY_Plane021]
  sketch-geometry (6):
    g0: LineSegment StartX=-0.55 StartY=3.04345 StartZ=0 EndX=9.55 EndY=3.04345 EndZ=0
    g1: LineSegment StartX=9.55 StartY=3.04345 StartZ=0 EndX=9.55 EndY=1.94345 EndZ=0
    g2: LineSegment StartX=9.55 StartY=1.94345 StartZ=0 EndX=0.55 EndY=1.94345 EndZ=0
    g3: LineSegment StartX=0.55 StartY=1.94345 StartZ=0 EndX=0.55 EndY=-7.05655 EndZ=0
    g4: LineSegment StartX=0.55 StartY=-7.05655 StartZ=0 EndX=-0.55 EndY=-7.05655 EndZ=0
    g5: LineSegment StartX=-0.55 StartY=-7.05655 StartZ=0 EndX=-0.55 EndY=3.04345 EndZ=0
  constraints (16):
    c: Horizontal(g0)
    c: Coincident(g0,g1)
    c: Vertical(g1)
    c: Coincident(g1,g2)
    c: Horizontal(g2)
    c: Coincident(g2,g3)
    c: Coincident(g3,g4)
    c: Coincident(g4,g5)
    c: Coincident(g5,g0)
    c: Vertical(g5)
    c: Equal(g4,g1)
    c: DistanceX(g0,g0) = 10.1
    c: DistanceY(g1,g1) = 1.1
    c: Equal(g5,g0)
    c: Vertical(g3)
    c: Symmetric(g3,g4,g-2)
FEATURE [PartDesign::Pocket] Pocket009
  BaseFeature = -> Pad011
  Direction = (0,0,-1)
  Length = 15
  Length2 = 100
  Profile = -> Sketch032
  Type = 1
FEATURE [Sketcher::SketchObject] Sketch035
  AttachmentOffset = pos=(0,0,-10) rot=(0,0,1;0rad)
  FullyConstrained = true
  MapMode = 5
  Placement = pos=(0,0,-10) rot=(0,0,1;0rad)
  Support = -> [XY_Plane021]
  sketch-geometry (6):
    g0: LineSegment StartX=0.55 StartY=2.15 StartZ=0 EndX=1.65 EndY=2.15 EndZ=0
    g1: LineSegment StartX=1.65 StartY=2.15 StartZ=0 EndX=1.65 EndY=-8.15 EndZ=0
    g2: LineSegment StartX=1.65 StartY=-8.15 StartZ=0 EndX=-8.45 EndY=-8.15 EndZ=0
    g3: LineSegment StartX=-8.45 StartY=-8.15 StartZ=0 EndX=-8.45 EndY=-7.05 EndZ=0
    g4: LineSegment StartX=-8.45 StartY=-7.05 StartZ=0 EndX=0.55 EndY=-7.05 EndZ=0
    g5: LineSegment StartX=0.55 StartY=-7.05 StartZ=0 EndX=0.55 EndY=2.15 EndZ=0
  constraints (18):
    c: Horizontal(g0)
    c: Coincident(g0,g1)
    c: Vertical(g1)
    c: Coincident(g1,g2)
    c: Horizontal(g2)
    c: Coincident(g2,g3)
    c: Coincident(g3,g4)
    c: Horizontal(g4)
    c: Coincident(g4,g5)
    c: Coincident(g5,g0)
    c: Equal(g0,g3)
    c: Vertical(g3)
    c: DistanceY(g1,g1) = 10.3
    c: DistanceX(g0,g0) = 1.1
    c: DistanceX(g2,g2) = 10.1
    c: Vertical(g5)
    c: DistanceX(g4) = 0.55
    c: DistanceY(g4) = -7.05
FEATURE [PartDesign::Pocket] Pocket010
  BaseFeature = -> Pocket009
  Direction = (0,0,-1)
  Length = 5
  Length2 = 100
  Profile = -> Sketch035
  Type = 0
FEATURE [Sketcher::SketchObject] Sketch043
  AttachmentOffset = pos=(0,0,-5) rot=(0,0,1;0rad)
  FullyConstrained = false
  MapMode = 5
  Placement = pos=(0,0,-5) rot=(0,0,1;0rad)
  Support = -> [XY_Plane021]
  sketch-geometry (8):
    g0: LineSegment StartX=-18.5595 StartY=-1.55437 StartZ=0 EndX=-15.3093 EndY=-1.55437 EndZ=0
    g1: LineSegment StartX=-14.3506 StartY=-5.55437 StartZ=0 EndX=-18.5595 EndY=-5.55437 EndZ=0
    g2: LineSegment StartX=-18.5595 StartY=-5.55437 StartZ=0 EndX=-18.5595 EndY=-1.55437 EndZ=0
    g3: ArcOfCircle CenterX=0 CenterY=0 CenterZ=0 NormalX=0 NormalY=0 NormalZ=1 AngleXU=0 Radius=15.388 StartAngle=3.24278 EndAngle=3.51088
    g4: ArcOfCircle CenterX=0 CenterY=0 CenterZ=0 NormalX=0 NormalY=0 NormalZ=1 AngleXU=0 Radius=15.388 StartAngle=0.101185 EndAngle=0.369292
    g5: LineSegment StartX=14.3506 StartY=5.55437 StartZ=0 EndX=18.5595 EndY=5.55437 EndZ=0
    g6: LineSegment StartX=18.5595 StartY=5.55437 StartZ=0 EndX=18.5595 EndY=1.55437 EndZ=0
    g7: LineSegment StartX=18.5595 StartY=1.55437 StartZ=0 EndX=15.3093 EndY=1.55437 EndZ=0
  constraints (19):
    c: Coincident(g1,g2)
    c: Coincident(g2,g0)
    c: Horizontal(g0)
    c: Horizontal(g1)
    c: Vertical(g2)
    c: Coincident(g3,g-1)
    c: Coincident(g3,g0)
    c: Coincident(g3,g1)
    c: DistanceY(g2,g2) = 4
    c: Coincident(g4,g3)
    c: Coincident(g4,g5)
    c: Coincident(g5,g6)
    c: Vertical(g6)
    c: Coincident(g6,g7)
    c: Coincident(g7,g4)
    c: Horizontal(g5)
    c: Horizontal(g7)
    c: Symmetric(g4,g0,g3)
    c: Symmetric(g5,g1,g3)
FEATURE [Sketcher::SketchObject] Sketch046
  FullyConstrained = false
  MapMode = 5
  Placement = pos=(0,0,0) rot=(0.57735,0.57735,0.57735;2.0944rad)
  Support = -> [YZ_Plane021]
  expr: Constraints[11] = Spreadsheet.r_outer
  expr: Constraints[12] = Spreadsheet.r_inner
  sketch-geometry (6):
    g0: LineSegment StartX=16.5 StartY=0 StartZ=0 EndX=16.5 EndY=-1.08055 EndZ=0
    g1: LineSegment StartX=16.5 StartY=-1.08055 StartZ=0 EndX=14.9353 EndY=-1.99693 EndZ=0
    g2: LineSegment StartX=14.9353 StartY=-1.99693 StartZ=0 EndX=14.625 EndY=-13.5266 EndZ=0
    g3: LineSegment StartX=14.625 StartY=-13.5266 StartZ=0 EndX=22.4612 EndY=-13.5266 EndZ=0
    g4: LineSegment StartX=22.4612 StartY=-13.5266 StartZ=0 EndX=22.4612 EndY=0 EndZ=0
    g5: LineSegment StartX=22.4612 StartY=0 StartZ=0 EndX=16.5 EndY=0 EndZ=0
  constraints (13):
    c: PointOnObject(g0,g-1)
    c: Vertical(g0)
    c: Coincident(g0,g1)
    c: Coincident(g1,g2)
    c: Coincident(g2,g3)
    c: Horizontal(g3)
    c: Coincident(g3,g4)
    c: Vertical(g4)
    c: Coincident(g4,g5)
    c: Horizontal(g5)
    c: Coincident(g0,g5)
    c: DistanceX(g0) = 16.5
    c: DistanceX(g2) = 14.625
FEATURE [PartDesign::Groove] Groove
  Angle = 360
  Axis = (-2e-16,3e-16,1)
  Base = (0,0,0)
  BaseFeature = -> Pocket010
  Profile = -> Sketch046
  ReferenceAxis = -> Sketch046 [V_Axis]
  Refine = true
FEATURE [PartDesign::Body] b_topBlockBase
  Group = -> [LCS_0002,Sketch031,Pad011,Sketch032,Pocket009,Sketch035,Pocket010,Sketch043,DatumPlane002,Sketch046,Groove]
  Origin = -> Origin021
  Tip = -> Groove
COMPONENT P10 — recipe-attached ("b_topBlockCap", modeled in this document).
Construction recipe (the document's own serialized feature program — sketch geometry with constraints, then the solid features built on it; lengths are millimeters unless a unit is written):

FEATURE [PartDesign::CoordinateSystem] LCS_0006
  AttacherType = Attacher::AttachEngine3D
  MapMode = 2
  Support = -> [X_Axis025]
FEATURE [Sketcher::SketchObject] Sketch050
  FullyConstrained = true
  MapMode = 5
  Support = -> [XY_Plane025]
  sketch-geometry (1):
    g0: Circle CenterX=0 CenterY=0 CenterZ=0 NormalX=0 NormalY=0 NormalZ=1 AngleXU=0 Radius=16.5
  constraints (2):
    c: Coincident(g0,g-1)
    c: Radius(g0) = 16.5
FEATURE [PartDesign::Pad] Pad015
  Direction = (1,1,1)
  Length = 2
  Length2 = 100
  Profile = -> Sketch050
  Type = 0
FEATURE [PartDesign::Fillet] Fillet
  Base = -> Pad015 [Edge3]
  BaseFeature = -> Pad015
  Radius = 1.3
  SupportTransform = false
  UseAllEdges = false
FEATURE [PartDesign::Body] b_topBlockCap
  Group = -> [LCS_0006,Sketch050,Pad015,Fillet]
  Origin = -> Origin025
  Tip = -> Fillet
COMPONENT P11 — recipe-attached ("b_pipe_dn32", modeled in this document).
Construction recipe (the document's own serialized feature program — sketch geometry with constraints, then the solid features built on it; lengths are millimeters unless a unit is written):

FEATURE [PartDesign::CoordinateSystem] LCS_0007
  AttacherType = Attacher::AttachEngine3D
  MapMode = 2
  Support = -> [X_Axis026]
FEATURE [Sketcher::SketchObject] Sketch051
  FullyConstrained = true
  MapMode = 5
  Support = -> [XY_Plane026]
  sketch-geometry (2):
    g0: Circle CenterX=0 CenterY=0 CenterZ=0 NormalX=0 NormalY=0 NormalZ=1 AngleXU=0 Radius=16.5
    g1: Circle CenterX=0 CenterY=0 CenterZ=0 NormalX=0 NormalY=0 NormalZ=1 AngleXU=0 Radius=14.5
  constraints (4):
    c: Coincident(g0,g-1)
    c: Radius(g0) = 16.5
    c: Coincident(g1,g0)
    c: Radius(g1) = 14.5
FEATURE [PartDesign::Pad] Pad016
  Direction = (0,0,1)
  Length = 480
  Length2 = 100
  Profile = -> Sketch051
  Refine = true
  Reversed = true
  Type = 0
FEATURE [PartDesign::Chamfer] Chamfer
  Angle = 45
  Base = -> Pad016 [Edge5]
  BaseFeature = -> Pad016
  ChamferType = 0
  FlipDirection = false
  Refine = true
  Size = 1
  Size2 = 1
  SupportTransform = false
  UseAllEdges = false
FEATURE [PartDesign::Body] b_tube_dn32  label="b_pipe_dn32"
  Group = -> [LCS_0007,Sketch051,Pad016,Chamfer]
  Origin = -> Origin026
  Tip = -> Chamfer
COMPONENT P12 — recipe-attached ("p_bottom_connector", modeled in this document).
Construction recipe (the document's own serialized feature program — sketch geometry with constraints, then the solid features built on it; lengths are millimeters unless a unit is written):

FEATURE [PartDesign::Plane] DatumPlane001
  AttachmentOffset = pos=(0,0,30) rot=(0,0,1;0rad)
  Length = 60
  MapMode = 2
  Placement = pos=(0,0,30) rot=(0,0,1;0rad)
  ResizeMode = 0
  Support = -> [X_Axis023]
  Width = 60
FEATURE [PartDesign::CoordinateSystem] LCS_0004
  AttacherType = Attacher::AttachEngine3D
  AttachmentOffset = pos=(0,0,2) rot=(1,0,0;0rad)
  MapMode = 2
  Placement = pos=(0,0,2) rot=(0,0,1;0rad)
  Support = -> [X_Axis023]
FEATURE [Sketcher::SketchObject] Sketch039
  FullyConstrained = true
  MapMode = 5
  Support = -> [XY_Plane023]
  sketch-geometry (6):
    g0: LineSegment StartX=5 StartY=5 StartZ=0 EndX=13.5 EndY=5 EndZ=0
    g1: LineSegment StartX=13.5 StartY=5 StartZ=0 EndX=13.5 EndY=-1.5 EndZ=0
    g2: LineSegment StartX=13.5 StartY=-1.5 StartZ=0 EndX=-1.5 EndY=-1.5 EndZ=0
    g3: LineSegment StartX=-1.5 StartY=-1.5 StartZ=0 EndX=-1.5 EndY=13.5 EndZ=0
    g4: LineSegment StartX=-1.5 StartY=13.5 StartZ=0 EndX=5 EndY=13.5 EndZ=0
    g5: LineSegment StartX=5 StartY=13.5 StartZ=0 EndX=5 EndY=5 EndZ=0
  constraints (18):
    c: Horizontal(g0)
    c: Coincident(g0,g1)
    c: Vertical(g1)
    c: Coincident(g1,g2)
    c: Coincident(g2,g3)
    c: Coincident(g3,g4)
    c: Horizontal(g4)
    c: Coincident(g4,g5)
    c: Coincident(g5,g0)
    c: Vertical(g5)
    c: Vertical(g3)
    c: Horizontal(g2)
    c: Equal(g3,g2)
    c: DistanceX(g2,g2) = 15
    c: Equal(g1,g4)
    c: DistanceX(g4,g4) = 6.5
    c: DistanceX(g2,g-1) = 1.5
    c: DistanceY(g2,g-1) = 1.5
FEATURE [PartDesign::Pad] Pad
  Direction = (1,1,1)
  Length = 30
  Length2 = 100
  Profile = -> Sketch039
  Type = 0
FEATURE [Sketcher::SketchObject] Sketch040
  FullyConstrained = true
  MapMode = 2
  Support = -> [X_Axis023]
  sketch-geometry (6):
    g0: LineSegment StartX=1 StartY=11.1 StartZ=0 EndX=2.1 EndY=11.1 EndZ=0
    g1: LineSegment StartX=2.1 StartY=11.1 StartZ=0 EndX=2.1 EndY=2.1 EndZ=0
    g2: LineSegment StartX=2.1 StartY=2.1 StartZ=0 EndX=11.1 EndY=2.1 EndZ=0
    g3: LineSegment StartX=11.1 StartY=2.1 StartZ=0 EndX=11.1 EndY=1 EndZ=0
    g4: LineSegment StartX=11.1 StartY=1 StartZ=0 EndX=1 EndY=1 EndZ=0
    g5: LineSegment StartX=1 StartY=1 StartZ=0 EndX=1 EndY=11.1 EndZ=0
  constraints (18):
    c: Coincident(g0,g1)
    c: Vertical(g1)
    c: Coincident(g1,g2)
    c: Horizontal(g2)
    c: Coincident(g2,g3)
    c: Vertical(g3)
    c: Coincident(g3,g4)
    c: Horizontal(g4)
    c: Coincident(g4,g5)
    c: Coincident(g5,g0)
    c: Vertical(g5)
    c: Horizontal(g0)
    c: Equal(g3,g0)
    c: Equal(g5,g4)
    c: DistanceX(g4,g4) = 10.1
    c: DistanceX(g0,g0) = 1.1
    c: DistanceY(g4) = 1
    c: DistanceX(g4) = 1
FEATURE [Sketcher::SketchObject] Sketch041
  FullyConstrained = true
  MapMode = 5
  Placement = pos=(0,0,30) rot=(0,0,1;0rad)
  Support = -> [DatumPlane001]
  sketch-geometry (6):
    g0: LineSegment StartX=0 StartY=10.1 StartZ=0 EndX=1.1 EndY=10.1 EndZ=0
    g1: LineSegment StartX=1.1 StartY=10.1 StartZ=0 EndX=1.1 EndY=1.1 EndZ=0
    g2: LineSegment StartX=1.1 StartY=1.1 StartZ=0 EndX=10.1 EndY=1.1 EndZ=0
    g3: LineSegment StartX=10.1 StartY=1.1 StartZ=0 EndX=10.1 EndY=0 EndZ=0
    g4: LineSegment StartX=10.1 StartY=0 StartZ=0 EndX=0 EndY=0 EndZ=0
    g5: LineSegment StartX=0 StartY=0 StartZ=0 EndX=0 EndY=10.1 EndZ=0
  constraints (17):
    c: Coincident(g0,g1)
    c: Vertical(g1)
    c: Coincident(g1,g2)
    c: Horizontal(g2)
    c: Coincident(g2,g3)
    c: Vertical(g3)
    c: Coincident(g3,g4)
    c: Horizontal(g4)
    c: Coincident(g4,g5)
    c: Coincident(g5,g0)
    c: Vertical(g5)
    c: Horizontal(g0)
    c: Equal(g3,g0)
    c: Equal(g5,g4)
    c: DistanceX(g4,g4) = 10.1
    c: DistanceX(g0,g0) = 1.1
    c: Coincident(g4,g-1)
FEATURE [PartDesign::Pocket] Pocket012
  BaseFeature = -> Pad
  Direction = (1,1,1)
  Length = 28
  Length2 = 100
  Profile = -> Sketch041
  Type = 0
FEATURE [PartDesign::Pocket] Pocket013
  BaseFeature = -> Pocket012
  Direction = (1,1,1)
  Length = 28
  Length2 = 100
  Profile = -> Sketch040
  Reversed = true
  Type = 0
FEATURE [Sketcher::SketchObject] Sketch042
  FullyConstrained = true
  MapMode = 5
  Support = -> [XY_Plane023]
  sketch-geometry (6):
    g0: LineSegment StartX=2 StartY=2.1 StartZ=0 EndX=3.1 EndY=2.1 EndZ=0
    g1: LineSegment StartX=3.1 StartY=2.1 StartZ=0 EndX=3.1 EndY=12.2 EndZ=0
    g2: LineSegment StartX=3.1 StartY=12.2 StartZ=0 EndX=-7 EndY=12.2 EndZ=0
    g3: LineSegment StartX=-7 StartY=12.2 StartZ=0 EndX=-7 EndY=11.1 EndZ=0
    g4: LineSegment StartX=-7 StartY=11.1 StartZ=0 EndX=2 EndY=11.1 EndZ=0
    g5: LineSegment StartX=2 StartY=11.1 StartZ=0 EndX=2 EndY=2.1 EndZ=0
  constraints (18):
    c: Horizontal(g0)
    c: Coincident(g0,g1)
    c: Vertical(g1)
    c: Coincident(g1,g2)
    c: Horizontal(g2)
    c: Coincident(g2,g3)
    c: Coincident(g3,g4)
    c: Horizontal(g4)
    c: Coincident(g4,g5)
    c: Coincident(g5,g0)
    c: Vertical(g5)
    c: Vertical(g3)
    c: Equal(g3,g0)
    c: Equal(g1,g2)
    c: DistanceY(g1,g1) = 10.1
    c: DistanceX(g0,g0) = 1.1
    c: DistanceY(g-1,g0) = 2.1
    c: DistanceX(g-1,g0) = 2
FEATURE [PartDesign::Pocket] Pocket014
  BaseFeature = -> Pocket013
  Direction = (0,0,-1)
  Length = 18
  Length2 = 100
  Profile = -> Sketch042
  Reversed = true
  Type = 0
FEATURE [PartDesign::Fillet] Fillet005
  Base = -> Pocket014 [Edge8,Edge32,Edge2,Edge5]
  BaseFeature = -> Pocket014
  Radius = 2
  SupportTransform = false
  UseAllEdges = false
FEATURE [PartDesign::Body] b_bottom_connector
  Group = -> [LCS_0004,Sketch039,Pad,DatumPlane001,Sketch040,Sketch041,Pocket012,Pocket013,Sketch042,Pocket014,Fillet005]
  Origin = -> Origin023
  Placement = pos=(0,0,0) rot=(0.707107,0.707107,0;3.14159rad)
  Tip = -> Fillet005
COMPONENT P13 — recipe-attached ("p_led_assembly", modeled in this document).
Construction recipe (the document's own serialized feature program — sketch geometry with constraints, then the solid features built on it; lengths are millimeters unless a unit is written):

FEATURE [PartDesign::CoordinateSystem] LCS_1005
  AttacherType = Attacher::AttachEngine3D
  MapMode = 2
  Support = -> [X_Axis032]
FEATURE [PartDesign::CoordinateSystem] LCS_1006
  AttacherType = Attacher::AttachEngine3D
  MapMode = 2
  Support = -> [X_Axis033]
FEATURE [Sketcher::SketchObject] Sketch056
  FullyConstrained = true
  MapMode = 5
  Support = -> [XY_Plane032]
  sketch-geometry (8):
    g0: LineSegment StartX=-100 StartY=5 StartZ=0 EndX=100 EndY=5 EndZ=0
    g1: LineSegment StartX=100 StartY=5 StartZ=0 EndX=100 EndY=-5 EndZ=0
    g2: LineSegment StartX=100 StartY=-5 StartZ=0 EndX=-100 EndY=-5 EndZ=0
    g3: LineSegment StartX=-100 StartY=-5 StartZ=0 EndX=-100 EndY=5 EndZ=0
    g4: Circle CenterX=-86 CenterY=0 CenterZ=0 NormalX=0 NormalY=0 NormalZ=1 AngleXU=0 Radius=1.5
    g5: Circle CenterX=86 CenterY=0 CenterZ=0 NormalX=0 NormalY=0 NormalZ=1 AngleXU=0 Radius=1.5
    g6: LineSegment StartX=-100 StartY=0 StartZ=0 EndX=-86 EndY=0 EndZ=0
    g7: LineSegment StartX=86 StartY=0 StartZ=0 EndX=100 EndY=0 EndZ=0
  constraints (22):
    c: Coincident(g0,g1)
    c: Coincident(g2,g3)
    c: Coincident(g3,g0)
    c: Horizontal(g2)
    c: Vertical(g1)
    c: Symmetric(g2,g0,g-1)
    c: DistanceX(g0,g0) = 200
    c: DistanceY(g1,g1) = 10
    c: PointOnObject(g5,g-1)
    c: PointOnObject(g6,g3)
    c: Horizontal(g6)
    c: DistanceX(g6,g6) = 14
    c: Equal(g4,g5)
    c: Diameter(g4) = 3
    c: Coincident(g1,g2)
    c: Coincident(g6,g4)
    c: Symmetric(g0,g0,g-2)
    c: Coincident(g7,g5)
    c: PointOnObject(g7,g1)
    c: Horizontal(g7)
    c: Equal(g7,g6)
    c: PointOnObject(g4,g-1)
FEATURE [PartDesign::Pad] Pad018
  Direction = (0,0,1)
  Length = 2
  Length2 = 10
  Profile = -> Sketch056
  ReferenceAxis = -> Sketch056 [N_Axis]
  Reversed = true
  Type = 0
FEATURE [PartDesign::Body] b_led_heatsink
  Group = -> [LCS_1005,Sketch056,Pad018]
  Origin = -> Origin032
  Tip = -> Pad018
FEATURE [Sketcher::SketchObject] Sketch057
  FullyConstrained = true
  MapMode = 5
  Support = -> [XY_Plane033]
  sketch-geometry (10):
    g0: ArcOfCircle CenterX=-79 CenterY=3.5 CenterZ=0 NormalX=0 NormalY=0 NormalZ=1 AngleXU=0 Radius=1 StartAngle=1.5708 EndAngle=3.14159
    g1: LineSegment StartX=-79 StartY=4.5 StartZ=0 EndX=79 EndY=4.5 EndZ=0
    g2: ArcOfCircle CenterX=79 CenterY=3.5 CenterZ=0 NormalX=0 NormalY=0 NormalZ=1 AngleXU=0 Radius=1 StartAngle=2e-16 EndAngle=1.5708
    g3: LineSegment StartX=80 StartY=3.5 StartZ=0 EndX=80 EndY=-3.5 EndZ=0
    g4: ArcOfCircle CenterX=79 CenterY=-3.5 CenterZ=0 NormalX=0 NormalY=0 NormalZ=1 AngleXU=0 Radius=1 StartAngle=4.71239 EndAngle=6.28319
    g5: LineSegment StartX=79 StartY=-4.5 StartZ=0 EndX=-79 EndY=-4.5 EndZ=0
    g6: ArcOfCircle CenterX=-79 CenterY=-3.5 CenterZ=0 NormalX=0 NormalY=0 NormalZ=1 AngleXU=0 Radius=1 StartAngle=3.14159 EndAngle=4.71239
    g7: LineSegment StartX=-80 StartY=-3.5 StartZ=0 EndX=-80 EndY=3.5 EndZ=0
    g8: GeomPoint X=-80 Y=4.5 Z=0
    g9: GeomPoint X=80 Y=-4.5 Z=0
  constraints (22):
    c: Tangent(g0,g1) = 1.5708
    c: Tangent(g1,g2) = 1.5708
    c: Tangent(g2,g3) = 1.5708
    c: Tangent(g3,g4) = 1.5708
    c: Tangent(g4,g5) = 1.5708
    c: Tangent(g5,g6) = 1.5708
    c: Tangent(g6,g7) = 1.5708
    c: Tangent(g7,g0) = 1.5708
    c: Horizontal(g1)
    c: Horizontal(g5)
    c: Vertical(g3)
    c: Vertical(g7)
    c: Equal(g0,g2)
    c: PointOnObject(g8,g1)
    c: PointOnObject(g8,g7)
    c: PointOnObject(g9,g3)
    c: PointOnObject(g9,g5)
    c: DistanceX(g0,g2) = 160
    c: Radius(g2) = 1
    c: DistanceY(g5,g0) = 9
    c: Symmetric(g6,g0,g-1)
    c: Symmetric(g4,g6,g-2)
FEATURE [PartDesign::Pad] Pad019
  Direction = (0,0,1)
  Length = 1
  Length2 = 10
  Profile = -> Sketch057
  ReferenceAxis = -> Sketch057 [N_Axis]
  Type = 0
FEATURE [PartDesign::Fillet] Fillet004
  Base = -> Pad019 [Edge13]
  BaseFeature = -> Pad019
  Radius = 0.9
  SupportTransform = false
  UseAllEdges = false
FEATURE [PartDesign::Body] b_led
  Group = -> [LCS_1006,Sketch057,Pad019,Fillet004]
  Origin = -> Origin033
  Tip = -> Fillet004
PROVENANCE & LICENSES
A FreeCAD (.FCStd) document from a public repository crawl; recipes are the document's own serialized feature recipes (and, for linked parts, companion documents' recipes).
License: as declared in the source repository (recorded in the dataset sidecar).
